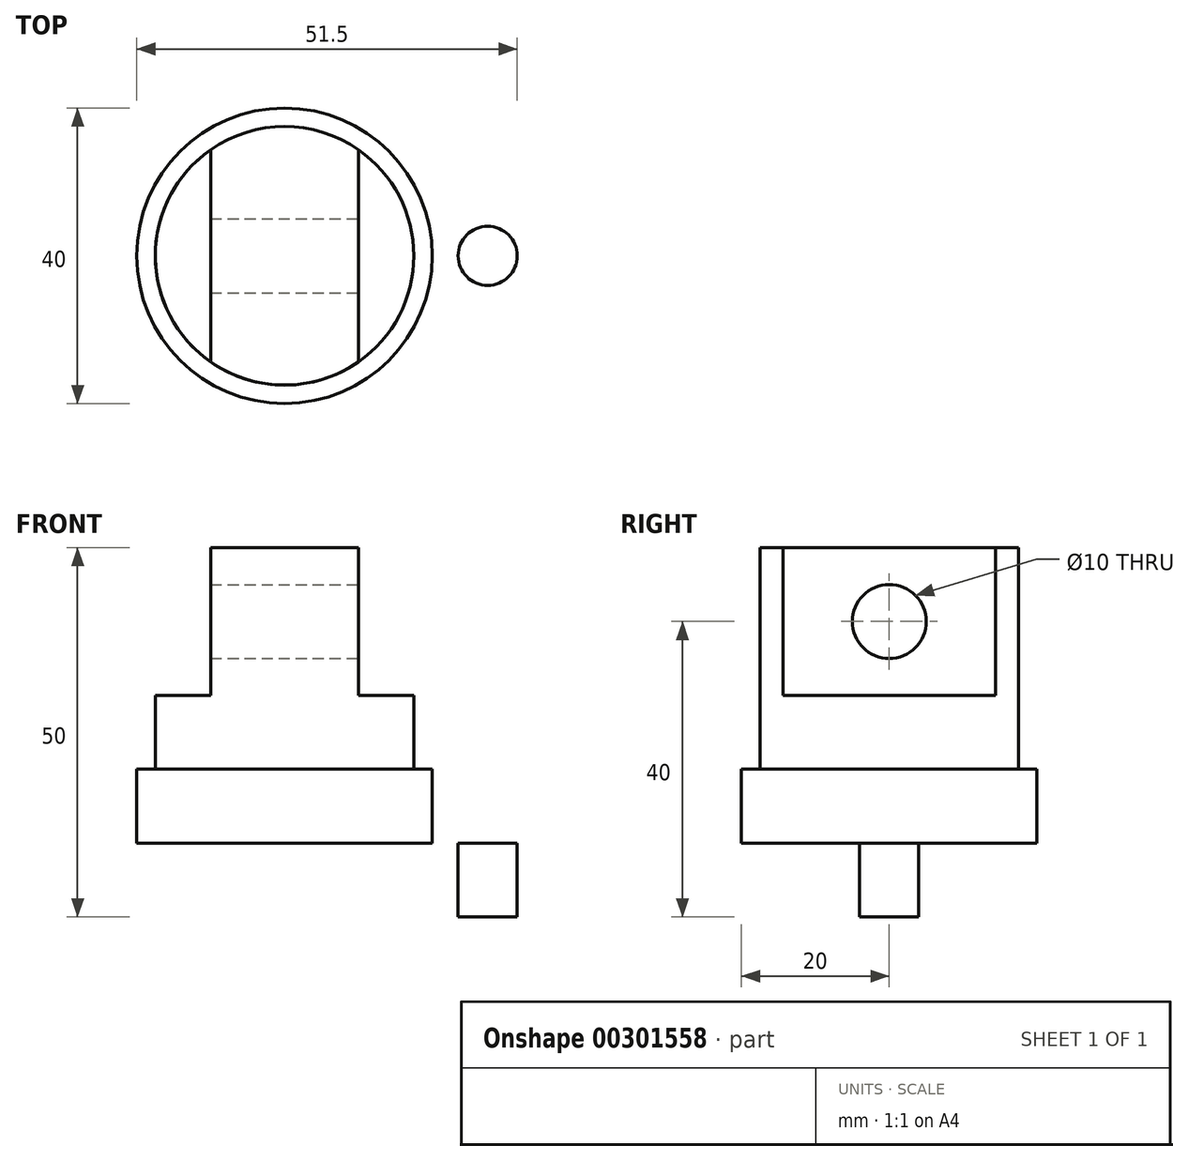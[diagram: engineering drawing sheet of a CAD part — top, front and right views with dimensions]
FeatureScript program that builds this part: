
annotation { "Feature Type Name" : "Feature", "Feature Type Description" : "" }
export const myFeature = defineFeature(function(context is Context, id is Id, definition is map)
    precondition{}
    {
        {
            var Q0;
            Q0=qCreatedBy(makeId("Top.planeOp"),FACE);
            var sketch = newSketch(context, id + "F0", { "sketchPlane" : qUnion([Q0])});
            skArc(sketch, "E0", {"start": v(-24.94, 28) * mm, "mid": v(-37.5, 0) * mm, "end": v(-24.94, -28) * mm});
            skLineSegment(sketch, "E1.bottom", {"start": v(-24.94, 28) * mm, "end": v(24.94, 28) * mm});
            skLineSegment(sketch, "E1.top", {"start": v(-24.94, -28) * mm, "end": v(24.94, -28) * mm});
            skArc(sketch, "E2.trimOffspring", {"start": v(24.94, -28) * mm, "mid": v(37.5, 0) * mm, "end": v(24.94, 28) * mm});
            skSolve(sketch);
        }
        {
            var Q0;
            Q0=makeQuery(id+"F0.imprint","IMPRINT",FACE,{"disambiguationData":[TD([[makeQuery(id+"F0.imprint","IMPRINT",EDGE,{"derivedFrom":sQuery(id+"F0.wireOp",EDGE,"E0")}),1.0]])]});
            extrude(context, id + "F1", {"entities" : qUnion([Q0]), "depth" : 10 * mm});
        }
        {
            var Q0;
            Q0=makeQuery(id+"F1.opExtrude","CAP_FACE",FACE,{"disambiguationData":[OSD([sQuery(id+"F0.wireOp",EDGE,"E0"),sQuery(id+"F0.wireOp",EDGE,"E1.bottom"),sQuery(id+"F0.wireOp",EDGE,"E1.top"),sQuery(id+"F0.wireOp",EDGE,"E2.trimOffspring")])],"isStart":false});
            var sketch = newSketch(context, id + "F2", { "sketchPlane" : qUnion([Q0])});
            skCircle(sketch, "E3", {"center": v(-27.5, 0) * mm, "radius": 4 * mm});
            skCircle(sketch, "E4.MirrorC", {"center": v(27.5, 0) * mm, "radius": 4 * mm});
            skSolve(sketch);
        }
        {
            var Q0;
            Q0=makeQuery(id+"F2.imprint","IMPRINT",FACE,{"disambiguationData":[TD([[makeQuery(id+"F2.imprint","IMPRINT",EDGE,{"derivedFrom":sQuery(id+"F2.wireOp",EDGE,"E3")}),1.0]])]});
            var Q1;
            Q1=makeQuery(id+"F2.imprint","IMPRINT",FACE,{"disambiguationData":[TD([[makeQuery(id+"F2.imprint","IMPRINT",EDGE,{"derivedFrom":sQuery(id+"F2.wireOp",EDGE,"E4.MirrorC")}),-1.0]])]});
            extrude(context, id + "F3", {"entities" : qUnion([Q0, Q1]), "operationType" : NewBodyOperationType.REMOVE, "endBound" : BoundingType.UP_TO_NEXT, "oppositeDirection" : true, "depth" : 25 * mm});
        }
        {
            var Q0;
            Q0=makeQuery(id+"F1.opExtrude","CAP_FACE",FACE,{"disambiguationData":[OSD([sQuery(id+"F0.wireOp",EDGE,"E0"),sQuery(id+"F0.wireOp",EDGE,"E1.bottom"),sQuery(id+"F0.wireOp",EDGE,"E1.top"),sQuery(id+"F0.wireOp",EDGE,"E2.trimOffspring")])],"isStart":false});
            var sketch = newSketch(context, id + "F4", { "sketchPlane" : qUnion([Q0])});
            skCircle(sketch, "E5", {"center": v(0, 0) * mm, "radius": 20 * mm});
            skSolve(sketch);
        }
        {
            var Q0;
            Q0=makeQuery(id+"F4.imprint","IMPRINT",FACE,{"disambiguationData":[TD([[makeQuery(id+"F4.imprint","IMPRINT",EDGE,{"derivedFrom":sQuery(id+"F4.wireOp",EDGE,"E5")}),1.0]])]});
            extrude(context, id + "F5", {"entities" : qUnion([Q0]), "operationType" : NewBodyOperationType.ADD, "depth" : 10 * mm});
        }
        {
            var Q0;
            Q0=makeQuery(id+"F5.opExtrude","CAP_FACE",FACE,{"disambiguationData":[OSD([sQuery(id+"F4.wireOp",EDGE,"E5")])],"isStart":false});
            var sketch = newSketch(context, id + "F6", { "sketchPlane" : qUnion([Q0])});
            skCircle(sketch, "E6", {"center": v(0, 0) * mm, "radius": 17.5 * mm});
            skSolve(sketch);
        }
        {
            var Q0;
            Q0=makeQuery(id+"F6.imprint","IMPRINT",FACE,{"disambiguationData":[TD([[makeQuery(id+"F6.imprint","IMPRINT",EDGE,{"derivedFrom":sQuery(id+"F6.wireOp",EDGE,"E6")}),1.0]])]});
            extrude(context, id + "F7", {"entities" : qUnion([Q0]), "operationType" : NewBodyOperationType.ADD, "depth" : 30 * mm});
        }
        {
            var Q0;
            Q0=makeQuery(id+"F7.opExtrude","CAP_FACE",FACE,{"disambiguationData":[OSD([sQuery(id+"F6.wireOp",EDGE,"E6")])],"isStart":false});
            var sketch = newSketch(context, id + "F8", { "sketchPlane" : qUnion([Q0])});
            skLineSegment(sketch, "E7.left", {"start": v(-10, 14.36) * mm, "end": v(-10, -14.36) * mm});
            skLineSegment(sketch, "E7.right", {"start": v(10, 14.36) * mm, "end": v(10, -14.36) * mm});
            skPoint(sketch, "E7.middle", {"position": v(0, 0) * mm});
            skArc(sketch, "E8", {"start": v(-10, 14.36) * mm, "mid": v(-17.5, 0) * mm, "end": v(-10, -14.36) * mm});
            skArc(sketch, "E9.trimOffspring", {"start": v(10, -14.36) * mm, "mid": v(17.5, 0) * mm, "end": v(10, 14.36) * mm});
            skSolve(sketch);
        }
        {
            var Q0;
            Q0=makeQuery(id+"F8.imprint","IMPRINT",FACE,{"disambiguationData":[TD([[makeQuery(id+"F8.imprint","IMPRINT",EDGE,{"derivedFrom":sQuery(id+"F8.wireOp",EDGE,"E7.left")}),-1.0]])]});
            var Q1;
            Q1=makeQuery(id+"F8.imprint","IMPRINT",FACE,{"disambiguationData":[TD([[makeQuery(id+"F8.imprint","IMPRINT",EDGE,{"derivedFrom":sQuery(id+"F8.wireOp",EDGE,"E7.right")}),1.0]])]});
            extrude(context, id + "F9", {"entities" : qUnion([Q0, Q1]), "operationType" : NewBodyOperationType.REMOVE, "oppositeDirection" : true, "depth" : 20 * mm});
        }
        {
            var Q0;
            Q0=makeQuery(id+"F9.boolean.opBoolean","COPY",FACE,{"derivedFrom":makeQuery(id+"F9.opExtrude","SWEPT_FACE",FACE,{"disambiguationData":[OSD([sQuery(id+"F8.wireOp",EDGE,"E7.right")])]})});
            var sketch = newSketch(context, id + "F10", { "sketchPlane" : qUnion([Q0])});
            skCircle(sketch, "E10", {"center": v(0, 40) * mm, "radius": 5 * mm});
            skPoint(sketch, "E10.centerSnap0", {"position": v(0, 30) * mm});
            skSolve(sketch);
        }
        {
            var Q0;
            Q0=makeQuery(id+"F10.imprint","IMPRINT",FACE,{"disambiguationData":[TD([[makeQuery(id+"F10.imprint","IMPRINT",EDGE,{"derivedFrom":sQuery(id+"F10.wireOp",EDGE,"E10")}),1.0]])]});
            extrude(context, id + "F11", {"entities" : qUnion([Q0]), "operationType" : NewBodyOperationType.REMOVE, "endBound" : BoundingType.UP_TO_NEXT, "oppositeDirection" : true, "depth" : 25 * mm});
        }
    });
